# Revit family: QSC SPA4-100 Amplifier Surface Mount
name_source: partatom
category: Generic Models
revit_build: Autodesk Revit 2014 (Build: 20130308_1515(x64)
units: mm (PartAtom-declared; Revit-internal decimal feet)

## types (3) — shared parameters
Default Elevation = 0.000"
Depth = 9.488"
Description = 4 Channel 100 Watt/Channel Amplfier
Face Depth = 0.079"
Heat Load Active = 103
Heat Load Standby = 33
Height = 1.730"
Manufacturer = QSC Audio Products, LLC
Manufacturer URL = http://www.qscaudio.com
Model = SPA4-100
Power Standby = 24
Product Documentation Link = http://www.qsc.com
Product Page URL = http://www.qsc.com
Regulatory Compliance = UL, CE, RoHS/WEEE, FCC Class B, UL 2043 with Plenum Kit Accessory
Sustainability Rating = Energy Star
URL = http://www.qsc.com
Voltage AC = 100-240 at 50-60 Hz
Weight Dimensional (kg) = 2.5
Weight Dimensional (lb) = 6.5
Weight Product (kg) = 1.4
Weight Product (lb) = 4
Width = 8.663"

## per-type parameters (varying)
| type | Current Draw | Power Active | Power Peak |
| SPA4-100 @ 100VAC | 1.7 | 130 | 170 |
| SPA4-100 @ 120VAC | 1.5 | 132 | 180 |
| SPA4-100 @ 230VAC | 0.8 | 184 | 184 |

## geometry (parser evidence)
native form markers: Blend x8, Sweep x9
no freeform markers — native parametric forms only
